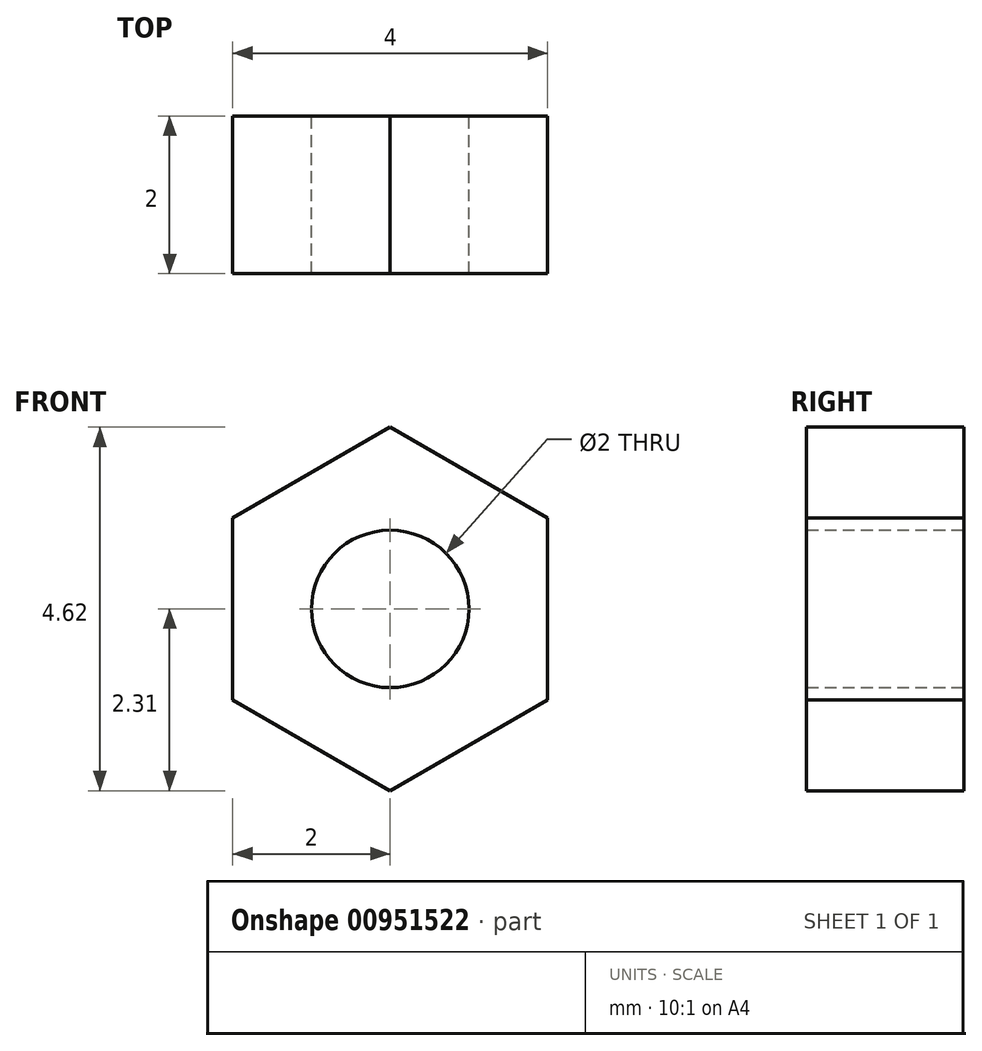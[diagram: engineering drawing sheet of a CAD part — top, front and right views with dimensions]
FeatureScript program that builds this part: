
annotation { "Feature Type Name" : "Feature", "Feature Type Description" : "" }
export const myFeature = defineFeature(function(context is Context, id is Id, definition is map)
    precondition{}
    {
        {
            var Q0;
            Q0=qCreatedBy(makeId("Front.planeOp"),FACE);
            var sketch = newSketch(context, id + "F0", { "sketchPlane" : qUnion([Q0])});
            skCircle(sketch, "E0", {"center": v(0, 0) * mm, "radius": 1 * mm});
            skCircle(sketch, "E1.cCircle", {"center": v(0, 0) * mm, "radius": 2 * mm, "construction": true});
            skLineSegment(sketch, "E1.0", {"start": v(-2, -1.15) * mm, "end": v(-2, 1.15) * mm});
            skLineSegment(sketch, "E1.1", {"start": v(-2, 1.15) * mm, "end": v(0, 2.3) * mm});
            skLineSegment(sketch, "E1.2", {"start": v(0, 2.3) * mm, "end": v(2, 1.15) * mm});
            skLineSegment(sketch, "E1.3", {"start": v(2, 1.15) * mm, "end": v(2, -1.15) * mm});
            skLineSegment(sketch, "E1.4", {"start": v(2, -1.15) * mm, "end": v(0, -2.3) * mm});
            skLineSegment(sketch, "E1.5", {"start": v(0, -2.3) * mm, "end": v(-2, -1.15) * mm});
            skPoint(sketch, "E1.0.midPoint", {"position": v(-2, 0) * mm});
            skSolve(sketch);
        }
        {
            var Q0;
            Q0=makeQuery(id+"F0.imprint","IMPRINT",FACE,{"disambiguationData":[TD([[makeQuery(id+"F0.imprint","IMPRINT",EDGE,{"derivedFrom":sQuery(id+"F0.wireOp",EDGE,"E0")}),-1.0]])]});
            extrude(context, id + "F1", {"entities" : qUnion([Q0]), "depth" : 2 * mm, "offsetDistance" : 25 * mm});
        }
    });
